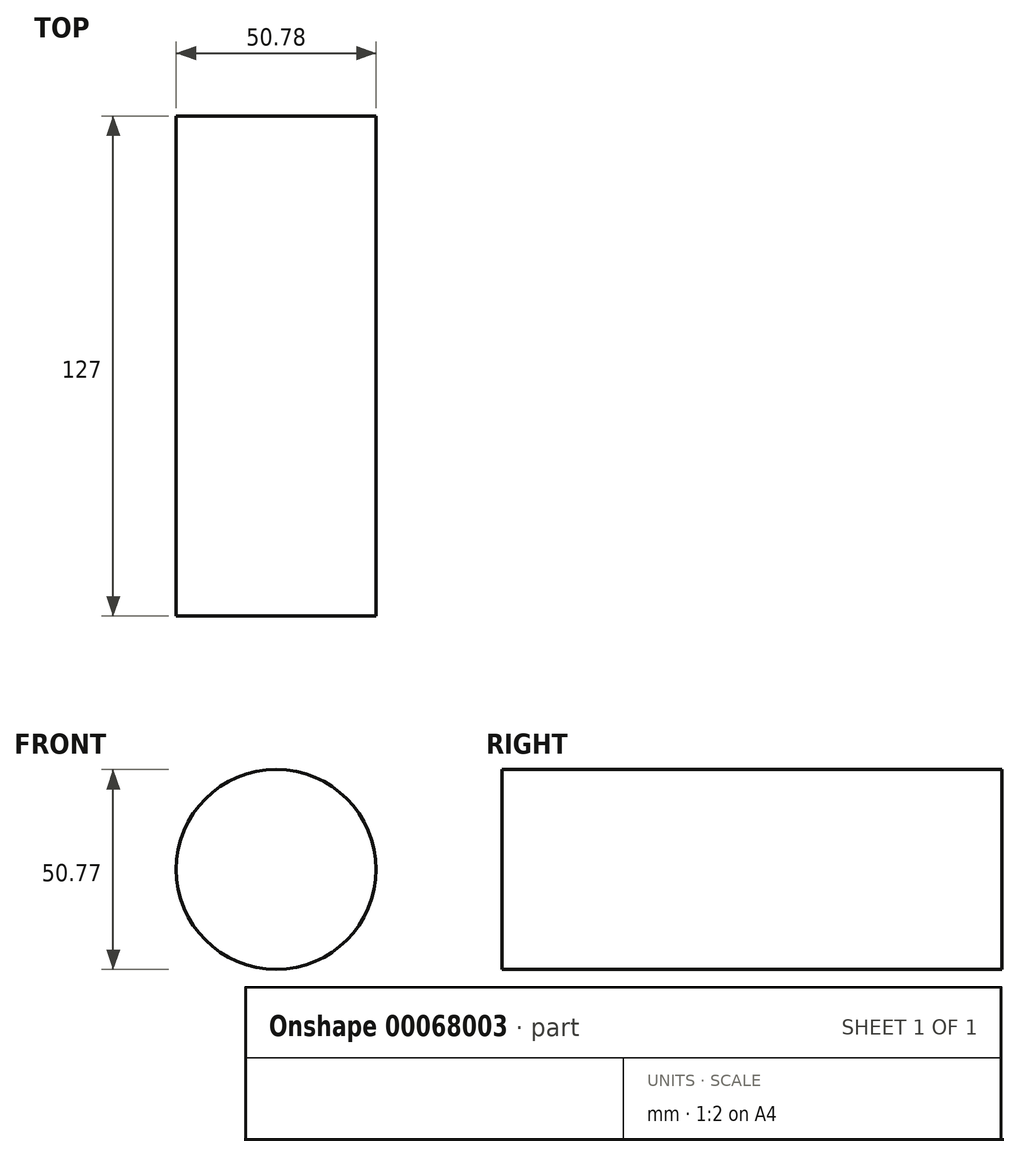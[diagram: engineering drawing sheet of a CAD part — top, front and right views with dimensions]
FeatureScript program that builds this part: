
annotation { "Feature Type Name" : "Feature", "Feature Type Description" : "" }
export const myFeature = defineFeature(function(context is Context, id is Id, definition is map)
    precondition{}
    {
        {
            var Q0;
            Q0=qCreatedBy(makeId("Front.planeOp"),FACE);
            var sketch = newSketch(context, id + "F0", { "sketchPlane" : qUnion([Q0])});
            skCircle(sketch, "E0", {"center": v(0, 43.12) * mm, "radius": 25.39 * mm});
            skSolve(sketch);
        }
        {
            var Q0;
            Q0=makeQuery(id+"F0.imprint","IMPRINT",FACE,{"disambiguationData":[TD([[makeQuery(id+"F0.imprint","IMPRINT",EDGE,{"derivedFrom":sQuery(id+"F0.wireOp",EDGE,"E0")}),1.0]])]});
            extrude(context, id + "F1", {"entities" : qUnion([Q0]), "depth" : 127 * mm});
        }
    });
